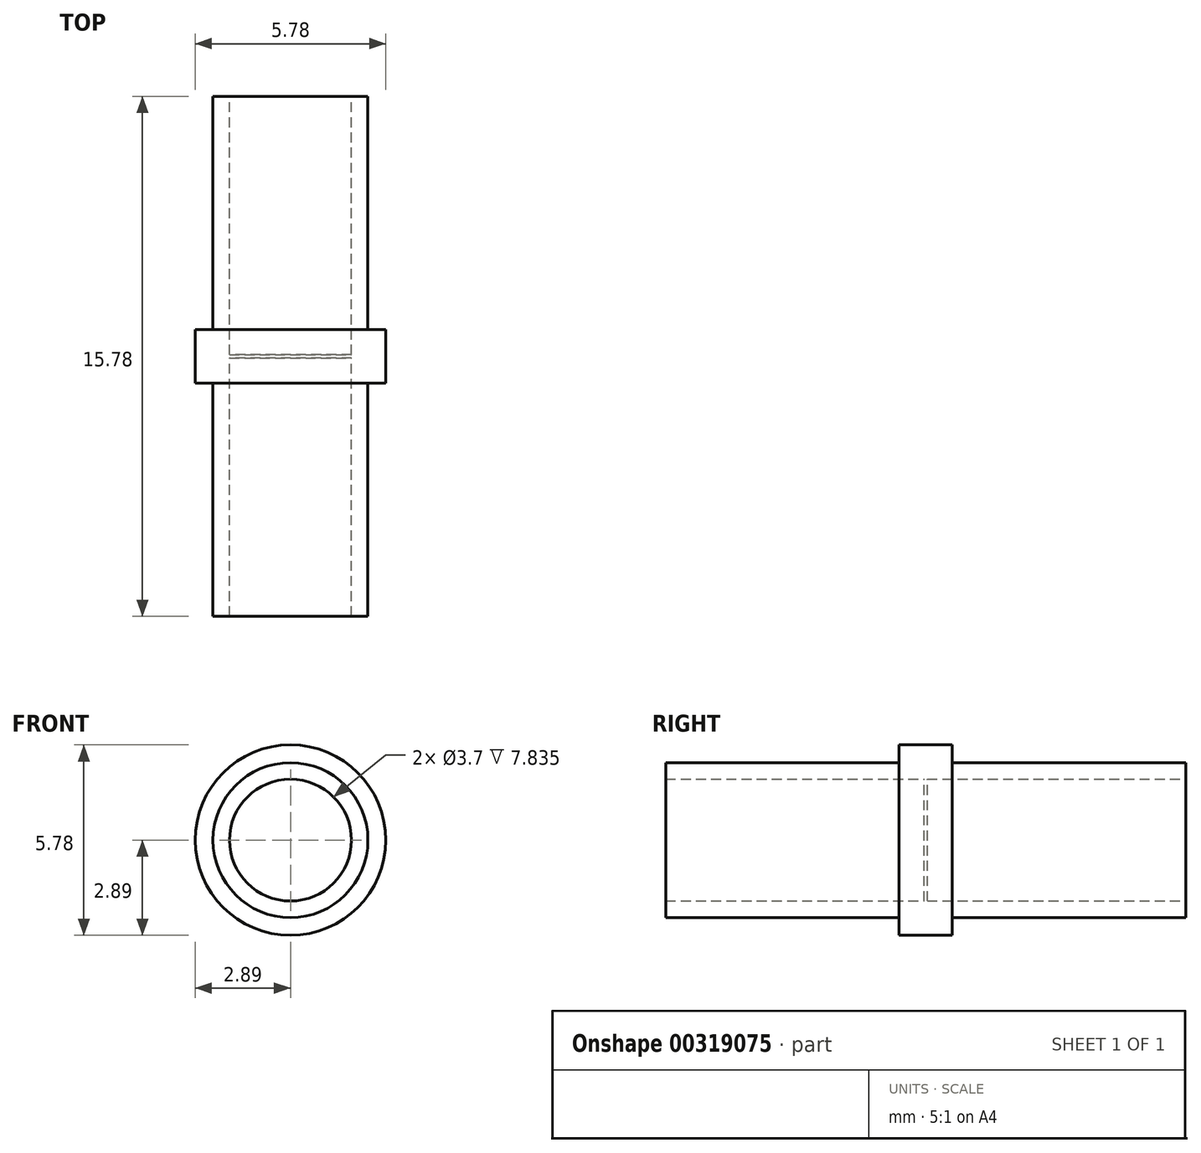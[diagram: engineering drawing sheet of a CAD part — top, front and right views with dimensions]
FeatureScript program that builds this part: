
annotation { "Feature Type Name" : "Feature", "Feature Type Description" : "" }
export const myFeature = defineFeature(function(context is Context, id is Id, definition is map)
    precondition{}
    {
        {
            var Q0;
            Q0=qCreatedBy(makeId("Front.planeOp"),FACE);
            var sketch = newSketch(context, id + "F0", { "sketchPlane" : qUnion([Q0])});
            skPoint(sketch, "E0", {"position": v(0, 0) * mm});
            skCircle(sketch, "E1", {"center": v(0, 0) * mm, "radius": 2.9 * mm});
            skCircle(sketch, "E2", {"center": v(0, 0) * mm, "radius": 2.35 * mm});
            skCircle(sketch, "E3", {"center": v(0, 0) * mm, "radius": 1.85 * mm});
            skSolve(sketch);
        }
        {
            var Q0;
            Q0=makeQuery(id+"F0.imprint","IMPRINT",FACE,{"disambiguationData":[TD([[makeQuery(id+"F0.imprint","IMPRINT",EDGE,{"derivedFrom":sQuery(id+"F0.wireOp",EDGE,"E1")}),1.0]])]});
            extrude(context, id + "F1", {"entities" : qUnion([Q0]), "endBound" : BoundingType.SYMMETRIC, "depth" : 1.62 * mm});
        }
        {
            var Q0;
            Q0=makeQuery(id+"F0.imprint","IMPRINT",FACE,{"disambiguationData":[TD([[makeQuery(id+"F0.imprint","IMPRINT",EDGE,{"derivedFrom":sQuery(id+"F0.wireOp",EDGE,"E2")}),1.0]])]});
            extrude(context, id + "F2", {"entities" : qUnion([Q0]), "operationType" : NewBodyOperationType.ADD, "endBound" : BoundingType.SYMMETRIC, "depth" : 15.77 * mm});
        }
        {
            var Q0;
            Q0=makeQuery(id+"F0.imprint","IMPRINT",FACE,{"disambiguationData":[TD([[makeQuery(id+"F0.imprint","IMPRINT",EDGE,{"derivedFrom":sQuery(id+"F0.wireOp",EDGE,"E3")}),1.0]])]});
            extrude(context, id + "F3", {"entities" : qUnion([Q0]), "operationType" : NewBodyOperationType.ADD, "endBound" : BoundingType.SYMMETRIC, "depth" : .1 * mm});
        }
    });
